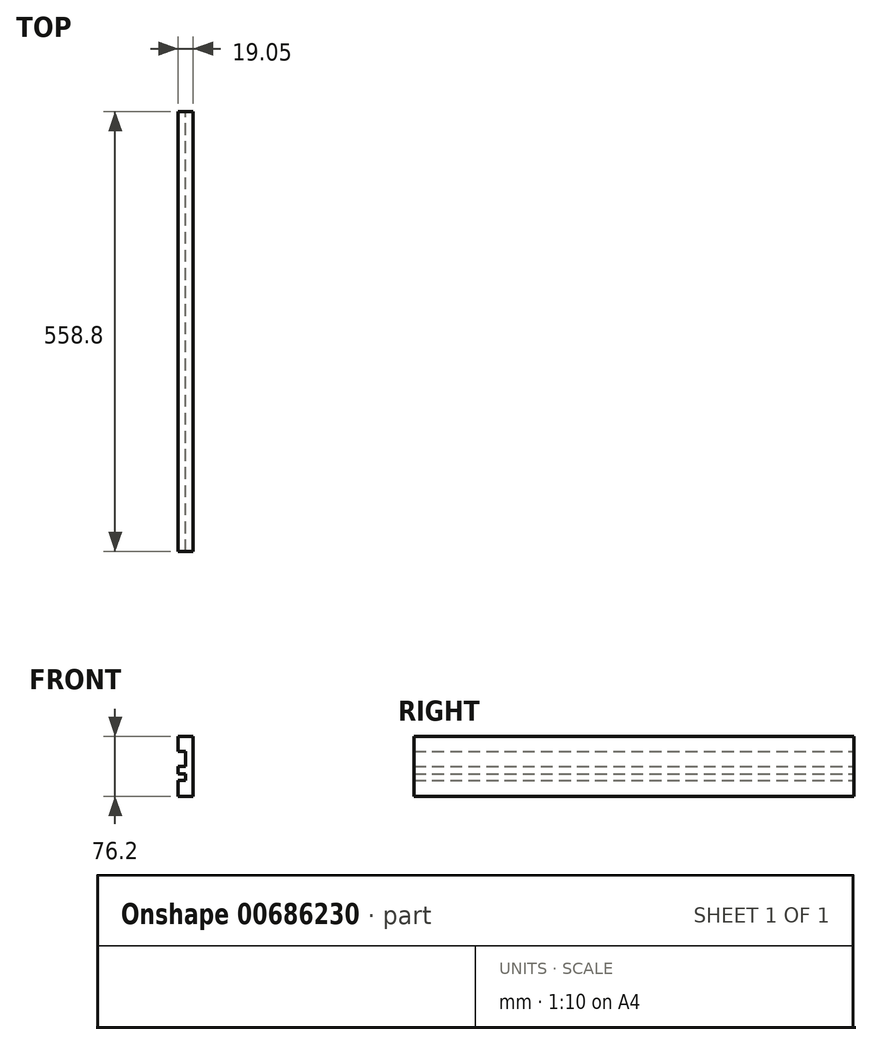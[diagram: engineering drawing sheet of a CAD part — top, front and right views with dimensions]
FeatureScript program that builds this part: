
annotation { "Feature Type Name" : "Feature", "Feature Type Description" : "" }
export const myFeature = defineFeature(function(context is Context, id is Id, definition is map)
    precondition{}
    {
        {
            var Q0;
            Q0=qCreatedBy(makeId("Front.planeOp"),FACE);
            var sketch = newSketch(context, id + "F0", { "sketchPlane" : qUnion([Q0])});
            skLineSegment(sketch, "E0.bottom", {"start": v(0, 0) * mm, "end": v(-19.05, 0) * mm});
            skLineSegment(sketch, "E0.top", {"start": v(0, -76.2) * mm, "end": v(-19.05, -76.2) * mm});
            skLineSegment(sketch, "E0.left", {"start": v(0, 0) * mm, "end": v(0, -19.05) * mm});
            skLineSegment(sketch, "E0.right", {"start": v(-19.05, 0) * mm, "end": v(-19.05, -19.05) * mm});
            skLineSegment(sketch, "E1", {"start": v(-9.52, -19.05) * mm, "end": v(-19.05, -19.05) * mm});
            skLineSegment(sketch, "E2", {"start": v(-9.52, -19.05) * mm, "end": v(-9.52, -38.1) * mm});
            skLineSegment(sketch, "E3", {"start": v(-19.05, -38.1) * mm, "end": v(-9.52, -38.1) * mm});
            skLineSegment(sketch, "E4.trimOffspring", {"start": v(0, -19.05) * mm, "end": v(0, -76.2) * mm});
            skLineSegment(sketch, "E5.trimOffspring", {"start": v(-19.05, -38.1) * mm, "end": v(-19.05, -47.62) * mm});
            skPoint(sketch, "E6.orphan", {"position": v(0, -38.1) * mm});
            skLineSegment(sketch, "E7", {"start": v(-19.05, -47.62) * mm, "end": v(-9.52, -47.62) * mm});
            skLineSegment(sketch, "E8", {"start": v(-9.52, -47.62) * mm, "end": v(-9.52, -55.56) * mm});
            skLineSegment(sketch, "E9", {"start": v(-9.52, -55.56) * mm, "end": v(-19.05, -55.56) * mm});
            skLineSegment(sketch, "E10.trimOffspring", {"start": v(-19.05, -55.56) * mm, "end": v(-19.05, -76.2) * mm});
            skSolve(sketch);
        }
        {
            var Q0;
            Q0 = qSketchRegion(id + "F0", true);
            extrude(context, id + "F1", {"entities" : qUnion([Q0]), "depth" : 558.8 * mm, "offsetDistance" : 25.4 * mm});
        }
    });
